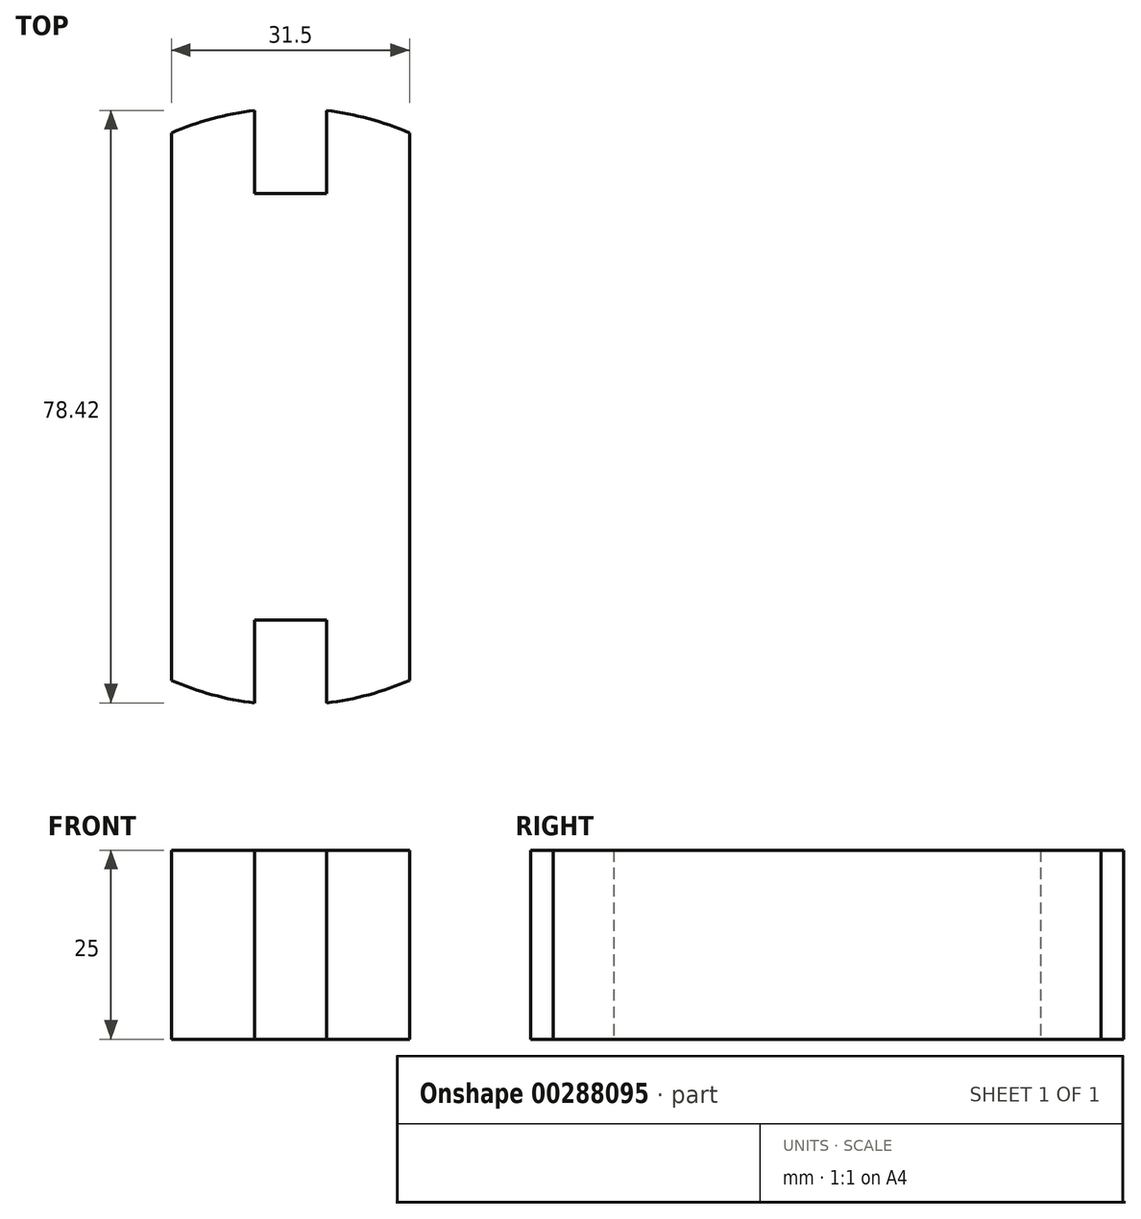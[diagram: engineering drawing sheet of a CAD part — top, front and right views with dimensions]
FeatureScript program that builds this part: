
annotation { "Feature Type Name" : "Feature", "Feature Type Description" : "" }
export const myFeature = defineFeature(function(context is Context, id is Id, definition is map)
    precondition{}
    {
        {
            var Q0;
            Q0=qCreatedBy(makeId("Top.planeOp"),FACE);
            var sketch = newSketch(context, id + "F0", { "sketchPlane" : qUnion([Q0])});
            skLineSegment(sketch, "E0.left", {"start": v(-15.75, 36.22) * mm, "end": v(-15.75, -36.22) * mm});
            skLineSegment(sketch, "E0.right", {"start": v(15.75, 36.22) * mm, "end": v(15.75, -36.22) * mm});
            skPoint(sketch, "E0.middle", {"position": v(0, 0) * mm});
            skArc(sketch, "E1", {"start": v(-15.75, -36.22) * mm, "mid": v(-10.36, -38.12) * mm, "end": v(-4.75, -39.21) * mm});
            skLineSegment(sketch, "E2", {"start": v(0, 0) * mm, "end": v(0, 46.5) * mm, "construction": true});
            skArc(sketch, "E3.trimOffspring", {"start": v(15.75, 36.22) * mm, "mid": v(10.36, 38.12) * mm, "end": v(4.75, 39.21) * mm});
            skLineSegment(sketch, "E4", {"start": v(-31.23, 0) * mm, "end": v(41.67, 0) * mm, "construction": true});
            skLineSegment(sketch, "E5", {"start": v(-4.75, 28.21) * mm, "end": v(4.75, 28.21) * mm});
            skLineSegment(sketch, "E6", {"start": v(4.75, 28.21) * mm, "end": v(4.75, 39.21) * mm});
            skLineSegment(sketch, "E7", {"start": v(-4.75, 28.21) * mm, "end": v(-4.75, 39.21) * mm});
            skPoint(sketch, "E8", {"position": v(0, 28.21) * mm});
            skLineSegment(sketch, "E9.MirrorCS", {"start": v(-4.75, -28.21) * mm, "end": v(-4.75, -39.21) * mm});
            skLineSegment(sketch, "E10.MirrorCS", {"start": v(-4.75, -28.21) * mm, "end": v(4.75, -28.21) * mm});
            skLineSegment(sketch, "E11.MirrorCS", {"start": v(4.75, -28.21) * mm, "end": v(4.75, -39.21) * mm});
            skArc(sketch, "E12.trimOffspring", {"start": v(-4.75, 39.21) * mm, "mid": v(-10.36, 38.12) * mm, "end": v(-15.75, 36.22) * mm});
            skArc(sketch, "E13.trimOffspring", {"start": v(4.75, -39.21) * mm, "mid": v(10.36, -38.12) * mm, "end": v(15.75, -36.22) * mm});
            skSolve(sketch);
        }
        {
            var Q0;
            Q0 = qSketchRegion(id + "F0", true);
            extrude(context, id + "F1", {"entities" : qUnion([Q0]), "depth" : 25 * mm});
        }
    });
